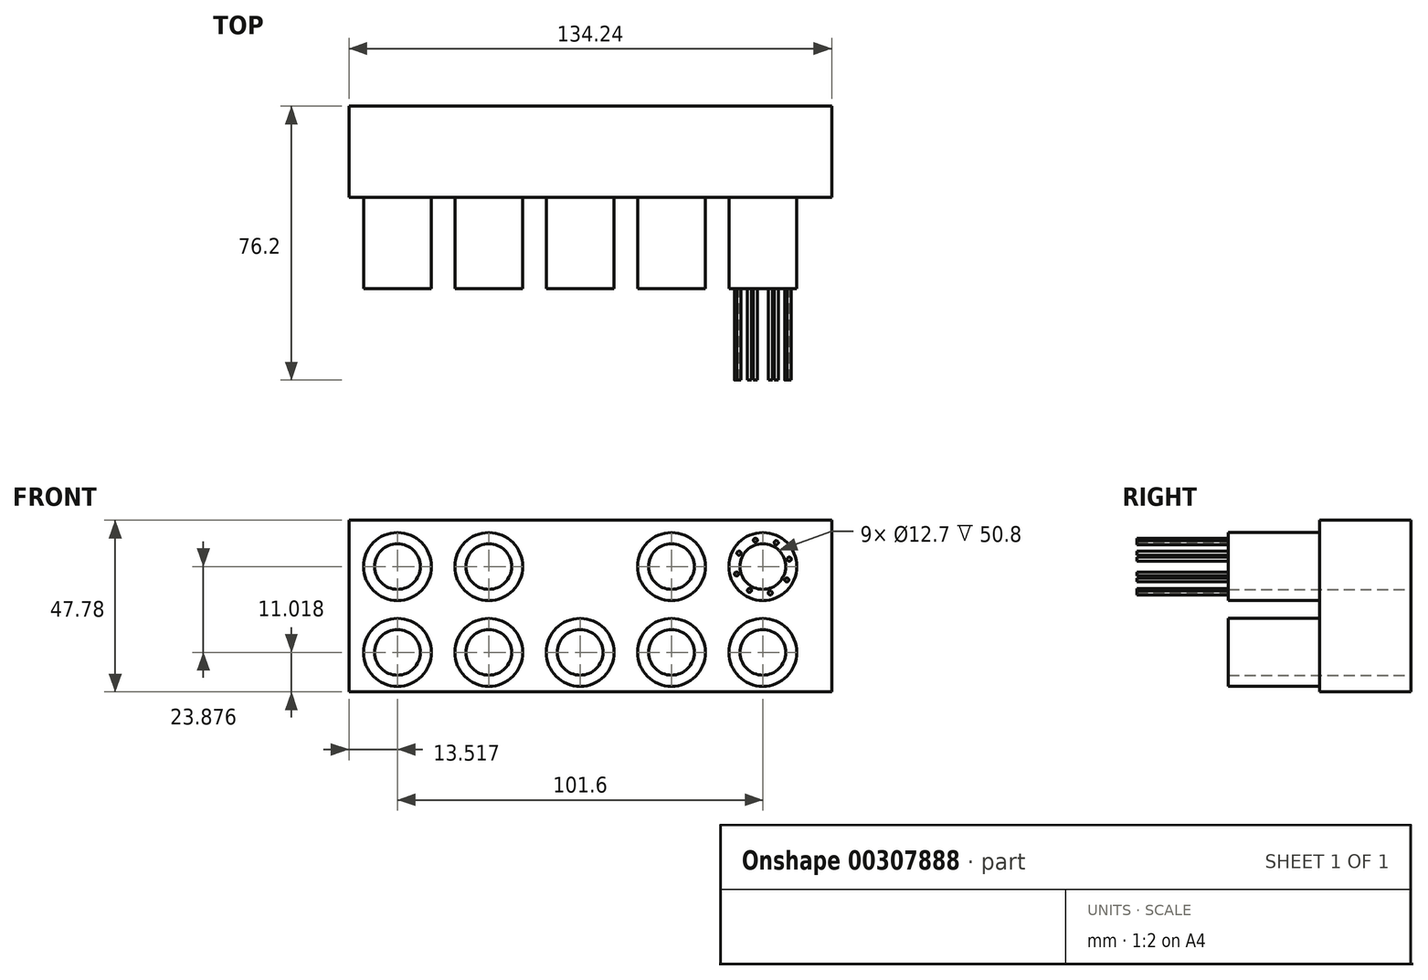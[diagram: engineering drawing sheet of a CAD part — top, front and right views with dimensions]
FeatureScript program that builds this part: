
annotation { "Feature Type Name" : "Feature", "Feature Type Description" : "" }
export const myFeature = defineFeature(function(context is Context, id is Id, definition is map)
    precondition{}
    {
        {
            var Q0;
            Q0=qCreatedBy(makeId("Front.planeOp"),FACE);
            var sketch = newSketch(context, id + "F0", { "sketchPlane" : qUnion([Q0])});
            skLineSegment(sketch, "E0.bottom", {"start": v(-60.36, 25) * mm, "end": v(73.88, 25) * mm});
            skLineSegment(sketch, "E0.top", {"start": v(-60.36, -22.8) * mm, "end": v(73.88, -22.8) * mm});
            skLineSegment(sketch, "E0.left", {"start": v(-60.36, 25) * mm, "end": v(-60.36, -22.8) * mm});
            skLineSegment(sketch, "E0.right", {"start": v(73.88, 25) * mm, "end": v(73.88, -22.8) * mm});
            skSolve(sketch);
        }
        {
            var Q0;
            Q0 = qSketchRegion(id + "F0", true);
            extrude(context, id + "F1", {"entities" : qUnion([Q0]), "depth" : 25.4 * mm});
        }
        {
            var Q0;
            Q0=makeQuery(id+"F1.opExtrude","CAP_FACE",FACE,{"disambiguationData":[OSD([sQuery(id+"F0.wireOp",EDGE,"E0.bottom"),sQuery(id+"F0.wireOp",EDGE,"E0.top"),sQuery(id+"F0.wireOp",EDGE,"E0.left"),sQuery(id+"F0.wireOp",EDGE,"E0.right")])],"isStart":false});
            var sketch = newSketch(context, id + "F2", { "sketchPlane" : qUnion([Q0])});
            skCircle(sketch, "E1", {"center": v(-46.84, 12.1) * mm, "radius": 6.35 * mm});
            skCircle(sketch, "E2", {"center": v(-46.84, 12.1) * mm, "radius": 9.45 * mm});
            skCircle(sketch, "E3.0.1.0", {"center": v(-46.84, -11.77) * mm, "radius": 6.35 * mm});
            skCircle(sketch, "E3.0.1.1", {"center": v(-46.84, -11.77) * mm, "radius": 9.45 * mm});
            skCircle(sketch, "E3.1.0.0", {"center": v(-21.44, 12.1) * mm, "radius": 6.35 * mm});
            skCircle(sketch, "E3.1.0.1", {"center": v(-21.44, 12.1) * mm, "radius": 9.45 * mm});
            skCircle(sketch, "E3.1.1.0", {"center": v(-21.44, -11.77) * mm, "radius": 6.35 * mm});
            skCircle(sketch, "E3.1.1.1", {"center": v(-21.44, -11.77) * mm, "radius": 9.45 * mm});
            skCircle(sketch, "E3.2.1.0", {"center": v(3.96, -11.77) * mm, "radius": 6.35 * mm});
            skCircle(sketch, "E3.2.1.1", {"center": v(3.96, -11.77) * mm, "radius": 9.45 * mm});
            skCircle(sketch, "E3.3.0.0", {"center": v(29.36, 12.1) * mm, "radius": 6.35 * mm});
            skCircle(sketch, "E3.3.0.1", {"center": v(29.36, 12.1) * mm, "radius": 9.45 * mm});
            skCircle(sketch, "E3.3.1.0", {"center": v(29.36, -11.77) * mm, "radius": 6.35 * mm});
            skCircle(sketch, "E3.3.1.1", {"center": v(29.36, -11.77) * mm, "radius": 9.45 * mm});
            skCircle(sketch, "E3.4.0.0", {"center": v(54.76, 12.1) * mm, "radius": 6.35 * mm});
            skCircle(sketch, "E3.4.0.1", {"center": v(54.76, 12.1) * mm, "radius": 9.45 * mm});
            skCircle(sketch, "E3.4.1.0", {"center": v(54.76, -11.77) * mm, "radius": 6.35 * mm});
            skCircle(sketch, "E3.4.1.1", {"center": v(54.76, -11.77) * mm, "radius": 9.45 * mm});
            skLineSegment(sketch, "E3.direction1", {"start": v(-46.84, 12.1) * mm, "end": v(-21.44, 12.1) * mm, "construction": true});
            skLineSegment(sketch, "E3.direction2", {"start": v(-46.84, 12.1) * mm, "end": v(-46.84, -11.77) * mm, "construction": true});
            skSolve(sketch);
        }
        {
            var Q0;
            Q0 = qSketchRegion(id + "F2", true);
            extrude(context, id + "F3", {"entities" : qUnion([Q0]), "operationType" : NewBodyOperationType.ADD, "depth" : 25.4 * mm});
        }
        {
            var Q0;
            Q0=makeQuery(id+"F3.boolean.opBoolean","SPLIT",FACE,{"disambiguationData":[TD([makeQuery(id+"F3.opExtrude","SWEPT_FACE",FACE,{"disambiguationData":[OSD([sQuery(id+"F2.wireOp",EDGE,"E1")])]})])],"derivedFrom":makeQuery(id+"F1.opExtrude","CAP_FACE",FACE,{"disambiguationData":[OSD([sQuery(id+"F0.wireOp",EDGE,"E0.bottom"),sQuery(id+"F0.wireOp",EDGE,"E0.top"),sQuery(id+"F0.wireOp",EDGE,"E0.left"),sQuery(id+"F0.wireOp",EDGE,"E0.right")])],"isStart":false})});
            var Q1;
            Q1=makeQuery(id+"F3.boolean.opBoolean","SPLIT",FACE,{"disambiguationData":[TD([makeQuery(id+"F3.opExtrude","SWEPT_FACE",FACE,{"disambiguationData":[OSD([sQuery(id+"F2.wireOp",EDGE,"E3.1.0.0")])]})])],"derivedFrom":makeQuery(id+"F1.opExtrude","CAP_FACE",FACE,{"disambiguationData":[OSD([sQuery(id+"F0.wireOp",EDGE,"E0.bottom"),sQuery(id+"F0.wireOp",EDGE,"E0.top"),sQuery(id+"F0.wireOp",EDGE,"E0.left"),sQuery(id+"F0.wireOp",EDGE,"E0.right")])],"isStart":false})});
            var Q2;
            Q2=makeQuery(id+"F3.boolean.opBoolean","SPLIT",FACE,{"disambiguationData":[TD([makeQuery(id+"F3.opExtrude","SWEPT_FACE",FACE,{"disambiguationData":[OSD([sQuery(id+"F2.wireOp",EDGE,"E3.3.0.0")])]})])],"derivedFrom":makeQuery(id+"F1.opExtrude","CAP_FACE",FACE,{"disambiguationData":[OSD([sQuery(id+"F0.wireOp",EDGE,"E0.bottom"),sQuery(id+"F0.wireOp",EDGE,"E0.top"),sQuery(id+"F0.wireOp",EDGE,"E0.left"),sQuery(id+"F0.wireOp",EDGE,"E0.right")])],"isStart":false})});
            var Q3;
            Q3=makeQuery(id+"F3.boolean.opBoolean","SPLIT",FACE,{"disambiguationData":[TD([makeQuery(id+"F3.opExtrude","SWEPT_FACE",FACE,{"disambiguationData":[OSD([sQuery(id+"F2.wireOp",EDGE,"E3.4.0.0")])]})])],"derivedFrom":makeQuery(id+"F1.opExtrude","CAP_FACE",FACE,{"disambiguationData":[OSD([sQuery(id+"F0.wireOp",EDGE,"E0.bottom"),sQuery(id+"F0.wireOp",EDGE,"E0.top"),sQuery(id+"F0.wireOp",EDGE,"E0.left"),sQuery(id+"F0.wireOp",EDGE,"E0.right")])],"isStart":false})});
            var Q4;
            Q4=makeQuery(id+"F3.boolean.opBoolean","SPLIT",FACE,{"disambiguationData":[TD([makeQuery(id+"F3.opExtrude","SWEPT_FACE",FACE,{"disambiguationData":[OSD([sQuery(id+"F2.wireOp",EDGE,"E3.4.1.0")])]})])],"derivedFrom":makeQuery(id+"F1.opExtrude","CAP_FACE",FACE,{"disambiguationData":[OSD([sQuery(id+"F0.wireOp",EDGE,"E0.bottom"),sQuery(id+"F0.wireOp",EDGE,"E0.top"),sQuery(id+"F0.wireOp",EDGE,"E0.left"),sQuery(id+"F0.wireOp",EDGE,"E0.right")])],"isStart":false})});
            var Q5;
            Q5=makeQuery(id+"F3.boolean.opBoolean","SPLIT",FACE,{"disambiguationData":[TD([makeQuery(id+"F3.opExtrude","SWEPT_FACE",FACE,{"disambiguationData":[OSD([sQuery(id+"F2.wireOp",EDGE,"E3.3.1.0")])]})])],"derivedFrom":makeQuery(id+"F1.opExtrude","CAP_FACE",FACE,{"disambiguationData":[OSD([sQuery(id+"F0.wireOp",EDGE,"E0.bottom"),sQuery(id+"F0.wireOp",EDGE,"E0.top"),sQuery(id+"F0.wireOp",EDGE,"E0.left"),sQuery(id+"F0.wireOp",EDGE,"E0.right")])],"isStart":false})});
            var Q6;
            Q6=makeQuery(id+"F3.boolean.opBoolean","SPLIT",FACE,{"disambiguationData":[TD([makeQuery(id+"F3.opExtrude","SWEPT_FACE",FACE,{"disambiguationData":[OSD([sQuery(id+"F2.wireOp",EDGE,"E3.2.1.0")])]})])],"derivedFrom":makeQuery(id+"F1.opExtrude","CAP_FACE",FACE,{"disambiguationData":[OSD([sQuery(id+"F0.wireOp",EDGE,"E0.bottom"),sQuery(id+"F0.wireOp",EDGE,"E0.top"),sQuery(id+"F0.wireOp",EDGE,"E0.left"),sQuery(id+"F0.wireOp",EDGE,"E0.right")])],"isStart":false})});
            var Q7;
            Q7=makeQuery(id+"F3.boolean.opBoolean","SPLIT",FACE,{"disambiguationData":[TD([makeQuery(id+"F3.opExtrude","SWEPT_FACE",FACE,{"disambiguationData":[OSD([sQuery(id+"F2.wireOp",EDGE,"E3.1.1.0")])]})])],"derivedFrom":makeQuery(id+"F1.opExtrude","CAP_FACE",FACE,{"disambiguationData":[OSD([sQuery(id+"F0.wireOp",EDGE,"E0.bottom"),sQuery(id+"F0.wireOp",EDGE,"E0.top"),sQuery(id+"F0.wireOp",EDGE,"E0.left"),sQuery(id+"F0.wireOp",EDGE,"E0.right")])],"isStart":false})});
            var Q8;
            Q8=makeQuery(id+"F3.boolean.opBoolean","SPLIT",FACE,{"disambiguationData":[TD([makeQuery(id+"F3.opExtrude","SWEPT_FACE",FACE,{"disambiguationData":[OSD([sQuery(id+"F2.wireOp",EDGE,"E3.0.1.0")])]})])],"derivedFrom":makeQuery(id+"F1.opExtrude","CAP_FACE",FACE,{"disambiguationData":[OSD([sQuery(id+"F0.wireOp",EDGE,"E0.bottom"),sQuery(id+"F0.wireOp",EDGE,"E0.top"),sQuery(id+"F0.wireOp",EDGE,"E0.left"),sQuery(id+"F0.wireOp",EDGE,"E0.right")])],"isStart":false})});
            extrude(context, id + "F4", {"entities" : qUnion([Q0, Q1, Q2, Q3, Q4, Q5, Q6, Q7, Q8]), "operationType" : NewBodyOperationType.REMOVE, "oppositeDirection" : true, "depth" : 25.4 * mm});
        }
        {
            var Q0;
            Q0=makeQuery(id+"F3.opExtrude","CAP_FACE",FACE,{"disambiguationData":[OSD([sQuery(id+"F2.wireOp",EDGE,"E3.4.0.0"),sQuery(id+"F2.wireOp",EDGE,"E3.4.0.1")])],"isStart":false});
            var sketch = newSketch(context, id + "F5", { "sketchPlane" : qUnion([Q0])});
            skCircle(sketch, "E4", {"center": v(52.7, 19.44) * mm, "radius": 0.56 * mm});
            skCircle(sketch, "E5.1.0", {"center": v(48.1, 15.83) * mm, "radius": 0.56 * mm});
            skCircle(sketch, "E5.2.0", {"center": v(47.42, 10.04) * mm, "radius": 0.56 * mm});
            skCircle(sketch, "E5.3.0", {"center": v(51.03, 5.46) * mm, "radius": 0.56 * mm});
            skCircle(sketch, "E5.4.0", {"center": v(56.82, 4.77) * mm, "radius": 0.56 * mm});
            skCircle(sketch, "E5.5.0", {"center": v(61.4, 8.38) * mm, "radius": 0.56 * mm});
            skCircle(sketch, "E5.6.0", {"center": v(62.1, 14.17) * mm, "radius": 0.56 * mm});
            skCircle(sketch, "E5.7.0", {"center": v(58.48, 18.75) * mm, "radius": 0.56 * mm});
            skPoint(sketch, "E5.center", {"position": v(54.76, 12.1) * mm});
            skSolve(sketch);
        }
        {
            var Q0;
            Q0=makeQuery(id+"F5.imprint","IMPRINT",FACE,{"disambiguationData":[TD([[makeQuery(id+"F5.imprint","IMPRINT",EDGE,{"derivedFrom":sQuery(id+"F5.wireOp",EDGE,"E5.1.0")}),1.0]])]});
            var Q1;
            Q1=makeQuery(id+"F5.imprint","IMPRINT",FACE,{"disambiguationData":[TD([[makeQuery(id+"F5.imprint","IMPRINT",EDGE,{"derivedFrom":sQuery(id+"F5.wireOp",EDGE,"E4")}),1.0]])]});
            var Q2;
            Q2=makeQuery(id+"F5.imprint","IMPRINT",FACE,{"disambiguationData":[TD([[makeQuery(id+"F5.imprint","IMPRINT",EDGE,{"derivedFrom":sQuery(id+"F5.wireOp",EDGE,"E5.7.0")}),1.0]])]});
            var Q3;
            Q3=makeQuery(id+"F5.imprint","IMPRINT",FACE,{"disambiguationData":[TD([[makeQuery(id+"F5.imprint","IMPRINT",EDGE,{"derivedFrom":sQuery(id+"F5.wireOp",EDGE,"E5.6.0")}),1.0]])]});
            var Q4;
            Q4=makeQuery(id+"F5.imprint","IMPRINT",FACE,{"disambiguationData":[TD([[makeQuery(id+"F5.imprint","IMPRINT",EDGE,{"derivedFrom":sQuery(id+"F5.wireOp",EDGE,"E5.5.0")}),1.0]])]});
            var Q5;
            Q5=makeQuery(id+"F5.imprint","IMPRINT",FACE,{"disambiguationData":[TD([[makeQuery(id+"F5.imprint","IMPRINT",EDGE,{"derivedFrom":sQuery(id+"F5.wireOp",EDGE,"E5.4.0")}),1.0]])]});
            var Q6;
            Q6=makeQuery(id+"F5.imprint","IMPRINT",FACE,{"disambiguationData":[TD([[makeQuery(id+"F5.imprint","IMPRINT",EDGE,{"derivedFrom":sQuery(id+"F5.wireOp",EDGE,"E5.3.0")}),1.0]])]});
            var Q7;
            Q7=makeQuery(id+"F5.imprint","IMPRINT",FACE,{"disambiguationData":[TD([[makeQuery(id+"F5.imprint","IMPRINT",EDGE,{"derivedFrom":sQuery(id+"F5.wireOp",EDGE,"E5.2.0")}),1.0]])]});
            extrude(context, id + "F6", {"entities" : qUnion([Q0, Q1, Q2, Q3, Q4, Q5, Q6, Q7]), "depth" : 25.4 * mm});
        }
    });
